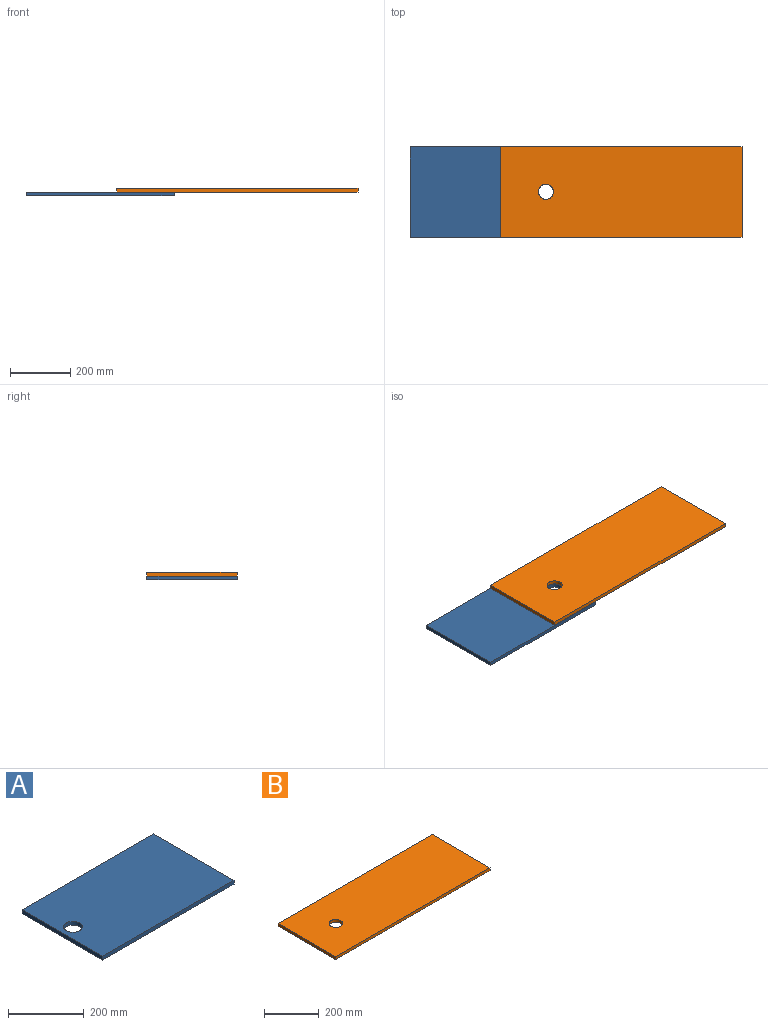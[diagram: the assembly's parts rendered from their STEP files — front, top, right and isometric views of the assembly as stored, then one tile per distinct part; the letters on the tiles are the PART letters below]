
ASSEMBLY  parts=2 mates=1
PART A: 7 faces, bbox 490x300x12.5 mm
  f0: plane 490x12.5mm, normal (0,1,0), area 6125mm2, adj f1,f4,f5,f6
  f1: plane 300x12.5mm, normal (-1,0,0), area 3750mm2, adj f0,f2,f5,f6
  f2: plane 490x12.5mm, normal (0,-1,0), area 6125mm2, adj f1,f4,f5,f6
  f3: cylinder r=25mm len=50mm, axis (0,0,-1), area 1963.5mm2, adj f5,f6
  f4: plane 300x12.5mm, normal (1,0,0), area 3750mm2, adj f0,f2,f5,f6
  f5: plane 490x300mm, normal (0,0,1), area 145036.5mm2, adj f0,f1,f2,f3,f4
  f6: plane 490x300mm, normal (0,0,-1), area 145036.5mm2, adj f0,f1,f2,f3,f4
PART B: 7 faces, bbox 800x300x12.5 mm
  f0: plane 800x12.5mm, normal (0,1,0), area 10000mm2, adj f1,f4,f5,f6
  f1: plane 300x12.5mm, normal (-1,0,0), area 3750mm2, adj f0,f2,f5,f6
  f2: plane 800x12.5mm, normal (0,-1,0), area 10000mm2, adj f1,f4,f5,f6
  f3: cylinder r=25mm len=50mm, axis (0,0,-1), area 1963.5mm2, adj f5,f6
  f4: plane 300x12.5mm, normal (1,0,0), area 3750mm2, adj f0,f2,f5,f6
  f5: plane 800x300mm, normal (0,0,1), area 238036.5mm2, adj f0,f1,f2,f3,f4
  f6: plane 800x300mm, normal (0,0,-1), area 238036.5mm2, adj f0,f1,f2,f3,f4
PLACE A rot(axis=(0,0,-1),179.9deg) t=(-453.21,17.38,6.56)mm
PLACE B t=(-167.7,-16.45,19.06)mm fixed
MATE revolute B.f3 <-> A.f3  axis (0,0,-1) through (-248.21,17.91,19.06)mm
